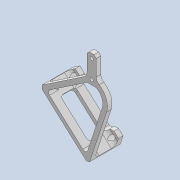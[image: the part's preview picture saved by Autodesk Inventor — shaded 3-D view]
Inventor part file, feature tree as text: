
AUTODESK INVENTOR PART (.ipt)
format: ipt  version: 2020 (Build 240168000, 168)  size: 310,272 bytes
history: native  units: mm
features: extrude x6, sketch x6, fillet x5, projected_geometry x5, other x4, reference x4, chamfer x3
ambient origin geometry x8: Origin, YZ Plane, XZ Plane, XY Plane, X Axis, Y Axis, Z Axis, Center Point
bodies: Solid1 (feature_tree)
feature tree (33):
  extrude  "Extrusion1"  Depth=6.0mm
  extrude  "Extrusion2"  Depth=2.0mm
  sketch  "Sketch3"  dims[d4=32.0mm d5=25.481807mm]
  other  "Work Point1"
  extrude  "Extrusion3"  Depth=25.481807mm
  extrude  "Extrusion4"  Depth=7.330383mm
  chamfer  "Chamfer1"  Distance=3.0mm
  extrude  "Extrusion5"  Depth=2.0mm
  fillet  "Fillet1"  Radius=7.6mm
  fillet  "Fillet2"  Radius=3.0mm
  chamfer  "Chamfer2"  Distance=2.5mm
  chamfer  "Chamfer3"  Distance=3.0mm
  fillet  "Fillet3"  Radius=14.5mm
  fillet  "Fillet4"  Radius=8.0mm
  extrude  "Extrusion6"  Depth=2.0mm
  fillet  "Fillet5"  Radius=6.0mm
  sketch  "Sketch1"  dims[d0=18.0mm d1=6.0mm]
  reference  "Reference1"
  reference  "Reference2"
  reference  "Reference3"
  reference  "Reference4"
  sketch  "Sketch2"  dims[d2=2.0mm d3=2.0mm]
  projected_geometry  "Projected Loop1"
  projected_geometry  "Projected Loop2"
  sketch  "Sketch4"  dims[d6=35.0mm d7=7.330383mm]
  projected_geometry  "Projected Loop3"
  projected_geometry  "Projected Loop4"
  sketch  "Sketch5"  dims[d8=8.0mm]
  sketch  "Sketch6"  dims[d9=3.0mm d10=3.0mm d11=0.078359mm d12=7.6mm d13=3.0mm d14=0.0mm d15=2.5mm d16=3.0mm d17=0.0mm d18=14.5mm d19=0.0mm d20=8.0mm d21=6.0mm d22=6.0mm d23=0.0mm d24=3.0mm d25=0.0mm d26=2.0mm d27=2.0mm d28=45.0deg d29=3.0mm d30=3.0mm d31=3.0mm d32=0.0mm d33=33.5mm d34=1.6mm d35=3.0mm d36=2.0mm d37=2.0mm d38=2.0mm d39=45.0deg d40=1.5mm d41=2.0mm d42=45.0deg d43=4.0mm d44=2.0mm d45=25.0mm d46=10.0mm d47=3.0mm d48=0.0mm d49=2.0mm]
  projected_geometry  "Projected Loop5"
  parser-record x1  (decoder bookkeeping rows leaked as tree rows — omitted from the tree; the rows remain in map.json)
  other  "driver_ass_1.iam"
  other  "stand_1:1"
note: 1 file-system path scrubbed to <path> (originals preserved in map.json)
